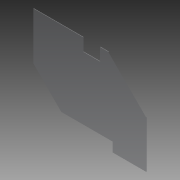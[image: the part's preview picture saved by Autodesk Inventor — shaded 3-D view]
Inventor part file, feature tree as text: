
AUTODESK INVENTOR PART (.ipt)
format: ipt  version: 2014 (Build 180170000, 170)  size: 83,968 bytes
history: native  units: in
note: dims shown in document units (in); Inventor stores cm internally (conversion verified against a paired STEP export)
features: extrude x1, sketch x1
ambient origin geometry x8: Origin, YZ Plane, XZ Plane, XY Plane, X Axis, Y Axis, Z Axis, Center Point
bodies: Solid1 (feature_tree)
feature tree (2):
  extrude  "Extrusion1"  Depth=5.91in
  sketch  "Sketch1"  dims[d2=0.0625in d3=0.0in d8=5.91in d28=9.0in d29=2.0in d30=5.5in d31=10.125in d32=0.75in d33=5.95in d34=1.5in]
